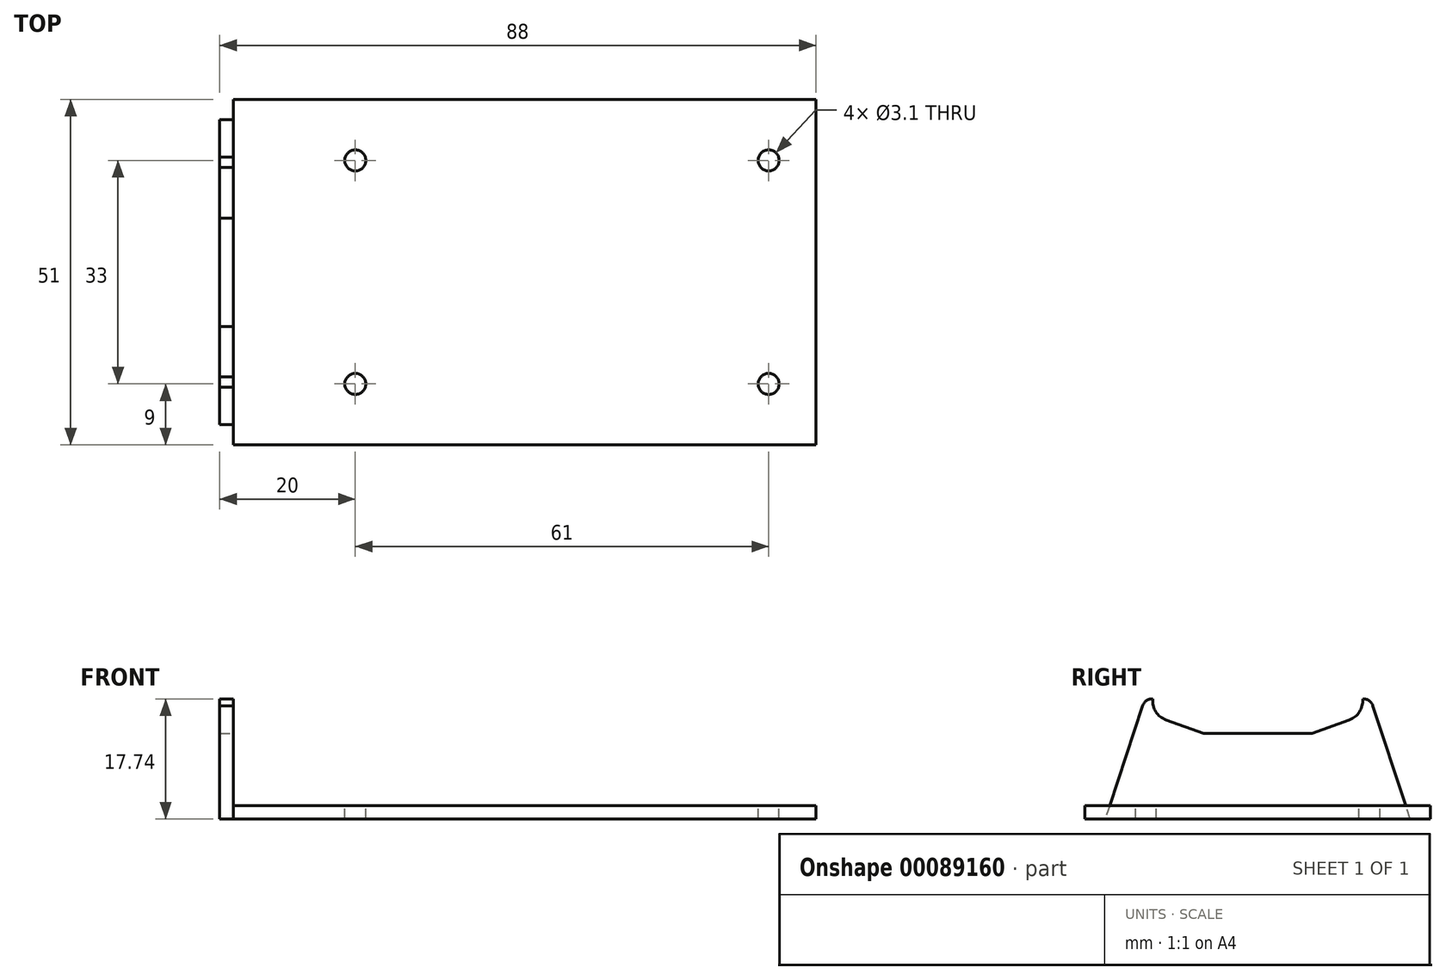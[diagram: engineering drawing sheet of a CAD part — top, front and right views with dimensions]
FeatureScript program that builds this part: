
annotation { "Feature Type Name" : "Feature", "Feature Type Description" : "" }
export const myFeature = defineFeature(function(context is Context, id is Id, definition is map)
    precondition{}
    {
        {
            var Q0;
            Q0=qCreatedBy(makeId("Top.planeOp"),FACE);
            var sketch = newSketch(context, id + "F0", { "sketchPlane" : qUnion([Q0])});
            skLineSegment(sketch, "E0.bottom", {"start": v(-43, 25.5) * mm, "end": v(43, 25.5) * mm});
            skLineSegment(sketch, "E0.top", {"start": v(-43, -25.5) * mm, "end": v(43, -25.5) * mm});
            skLineSegment(sketch, "E0.left", {"start": v(-43, 25.5) * mm, "end": v(-43, -25.5) * mm});
            skLineSegment(sketch, "E0.right", {"start": v(43, 25.5) * mm, "end": v(43, -25.5) * mm});
            skPoint(sketch, "E0.middle", {"position": v(0, 0) * mm});
            skSolve(sketch);
        }
        {
            var Q0;
            Q0 = qSketchRegion(id + "F0", true);
            extrude(context, id + "F1", {"entities" : qUnion([Q0]), "depth" : 2 * mm});
        }
        {
            var Q0;
            Q0=makeQuery(id+"F1.opExtrude","SWEPT_FACE",FACE,{"disambiguationData":[OSD([sQuery(id+"F0.wireOp",EDGE,"E0.left")])]});
            var sketch = newSketch(context, id + "F2", { "sketchPlane" : qUnion([Q0])});
            skLineSegment(sketch, "E1", {"start": v(0, 12.67) * mm, "end": v(8, 12.67) * mm});
            skLineSegment(sketch, "E2", {"start": v(-8, 12.67) * mm, "end": v(0, 12.67) * mm});
            skArc(sketch, "E3", {"start": v(13.5, 14.62) * mm, "mid": v(15.03, 15.84) * mm, "end": v(15.49, 17.74) * mm});
            skArc(sketch, "E4", {"start": v(-15.49, 17.74) * mm, "mid": v(-15.03, 15.84) * mm, "end": v(-13.5, 14.62) * mm});
            skLineSegment(sketch, "E5", {"start": v(-8, 12.67) * mm, "end": v(-13.5, 14.62) * mm});
            skLineSegment(sketch, "E6", {"start": v(8, 12.67) * mm, "end": v(13.5, 14.62) * mm});
            skLineSegment(sketch, "E7", {"start": v(16, 17.24) * mm, "end": v(16, 17.24) * mm});
            skPoint(sketch, "E8.end.orphan", {"position": v(0, 22.4) * mm});
            skLineSegment(sketch, "E9", {"start": v(-22.5, 0) * mm, "end": v(22.5, 0) * mm});
            skLineSegment(sketch, "E10", {"start": v(16.99, 16.74) * mm, "end": v(22.5, 0) * mm});
            skLineSegment(sketch, "E11", {"start": v(16.99, 17.74) * mm, "end": v(16.99, 16.74) * mm});
            skLineSegment(sketch, "E12", {"start": v(-22.5, 0) * mm, "end": v(-16.99, 16.74) * mm});
            skLineSegment(sketch, "E13", {"start": v(-16.99, 16.74) * mm, "end": v(-16.99, 17.74) * mm});
            skLineSegment(sketch, "E14", {"start": v(-15.49, 17.74) * mm, "end": v(-16.99, 17.74) * mm});
            skLineSegment(sketch, "E15", {"start": v(15.49, 17.74) * mm, "end": v(16.99, 17.74) * mm});
            skSolve(sketch);
        }
        {
            var Q0;
            {var subQ0=sQuery(id+"F0.wireOp",EDGE,"E0.left");Q0=makeQuery(id+"FjVLXSUkVL4fXL9_1.boolean.opBoolean","MERGE",FACE,{"derivedFrom":[makeQuery(id+"F1.opExtrude","CAP_FACE",FACE,{"disambiguationData":[OSD([sQuery(id+"F0.wireOp",EDGE,"E0.bottom"),sQuery(id+"F0.wireOp",EDGE,"E0.top"),subQ0,sQuery(id+"F0.wireOp",EDGE,"E0.right")])],"isStart":false}),makeQuery(id+"FjVLXSUkVL4fXL9_1.opExtrude","SWEPT_FACE",FACE,{"disambiguationData":[OSD([subQ0])]})]});}
            var sketch = newSketch(context, id + "F3", { "sketchPlane" : qUnion([Q0])});
            skCircle(sketch, "E16", {"center": v(-25, 16.5) * mm, "radius": 1.55 * mm});
            skCircle(sketch, "E17", {"center": v(-25, -16.5) * mm, "radius": 1.55 * mm});
            skCircle(sketch, "E18", {"center": v(36, 16.5) * mm, "radius": 1.55 * mm});
            skCircle(sketch, "E19", {"center": v(36, -16.5) * mm, "radius": 1.55 * mm});
            skSolve(sketch);
        }
        {
            var Q0;
            Q0 = qSketchRegion(id + "F3", true);
            extrude(context, id + "F4", {"entities" : qUnion([Q0]), "operationType" : NewBodyOperationType.REMOVE, "oppositeDirection" : true, "depth" : 25.4 * mm});
        }
        {
            var Q0;
            Q0 = qSketchRegion(id + "F2", true);
            var Q1;
            Q1=makeQuery(id+"F2.imprint","IMPRINT",FACE,{"disambiguationData":[TD([[makeQuery(id+"F2.imprint","IMPRINT",EDGE,{"derivedFrom":sQuery(id+"F2.wireOp",EDGE,"E1")}),-1.0]])]});
            extrude(context, id + "F5", {"entities" : qUnion([Q0, Q1]), "operationType" : NewBodyOperationType.ADD, "depth" : 2 * mm});
        }
        {
            var Q0;
            Q0=makeQuery(id+"F5.opExtrude","SWEPT_EDGE",EDGE,{"disambiguationData":[OSD([sQuery(id+"F2.wireOp",EDGE,"E11"),sQuery(id+"F2.wireOp",EDGE,"E15")])]});
            var Q1;
            Q1=makeQuery(id+"F5.opExtrude","SWEPT_EDGE",EDGE,{"disambiguationData":[OSD([sQuery(id+"F2.wireOp",EDGE,"E13"),sQuery(id+"F2.wireOp",EDGE,"E14")])]});
            fillet(context, id + "F6", {"entities" : qUnion([Q0, Q1]), "radius" : 1.5 * mm, "tangentPropagation" : true, "allowEdgeOverflow" : false});
        }
    });
